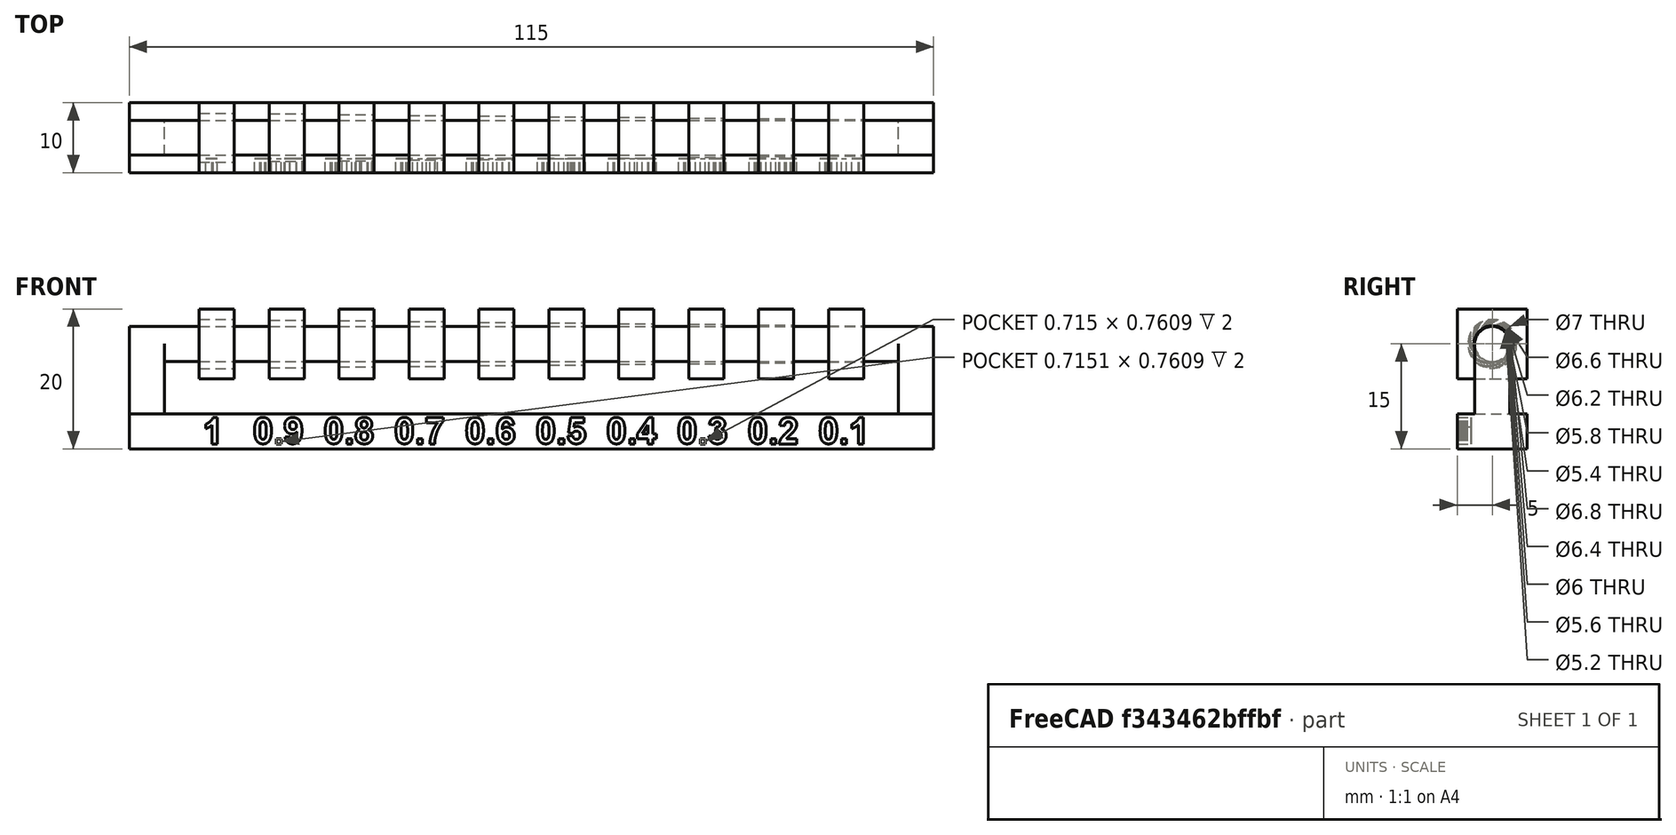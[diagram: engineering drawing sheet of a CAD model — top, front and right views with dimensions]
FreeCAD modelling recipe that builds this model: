
FCSTD DOCUMENT  (FreeCAD 0.18.3R)
Label: clearance
License: All rights reserved
LicenseURL: http://en.wikipedia.org/wiki/All_rights_reserved
objects: Part::Box×13, Part::Cylinder×11, Part::Cut×11, Part::MultiFuse×1, Part::Part2DObjectPython×1, Part::Extrusion×1
note: 38 computed .brp shape members not serialized (recipe doc carries the construction recipe); baked Part::Feature solids carry a one-line shape summary decoded from their .brp

FEATURE [Part::Box] Box  label="leg 0"
  AttacherType = Attacher::AttachEngine3D
  Height = 10
  Length = 5
  Width = 5
FEATURE [Part::Cylinder] Cylinder  label="axel"
  Angle = 360
  AttacherType = Attacher::AttachEngine3D
  Height = 115
  Placement = pos=(0,2.5,10) rot=(0,1,0;1.5708rad)
  Radius = 2.5
FEATURE [Part::Box] Box001  label="leg 1"
  AttacherType = Attacher::AttachEngine3D
  Height = 10
  Length = 5
  Placement = pos=(110,0,0) rot=(0,0,1;0rad)
  Width = 5
FEATURE [Part::Box] Box002  label="1 body"
  AttacherType = Attacher::AttachEngine3D
  Height = 10
  Length = 5
  Placement = pos=(10,-2.5,5) rot=(0,0,1;0rad)
  Width = 10
FEATURE [Part::Cylinder] Cylinder001  label="1 clearance"
  Angle = 360
  AttacherType = Attacher::AttachEngine3D
  Height = 115
  Placement = pos=(0,2.5,10) rot=(0,1,0;1.5708rad)
  Radius = 3.5
FEATURE [Part::Cut] Cut  label="1"
  Base = -> Box002
  Tool = -> Cylinder001
FEATURE [Part::Box] Box003  label="base"
  AttacherType = Attacher::AttachEngine3D
  Height = 5
  Length = 115
  Placement = pos=(0,-2.5,-5) rot=(0,0,1;0rad)
  Width = 10
FEATURE [Part::Box] Box004  label="0.8 body"
  AttacherType = Attacher::AttachEngine3D
  Height = 10
  Length = 5
  Placement = pos=(30,-2.5,5) rot=(0,0,1;0rad)
  Width = 10
FEATURE [Part::Cylinder] Cylinder002  label="0.8 clearance"
  Angle = 360
  AttacherType = Attacher::AttachEngine3D
  Height = 115
  Placement = pos=(0,2.5,10) rot=(0,1,0;1.5708rad)
  Radius = 3.3
FEATURE [Part::Cut] Cut001  label="0.8"
  Base = -> Box004
  Tool = -> Cylinder002
FEATURE [Part::Box] Box005  label="0.6 body"
  AttacherType = Attacher::AttachEngine3D
  Height = 10
  Length = 5
  Placement = pos=(50,-2.5,5) rot=(0,0,1;0rad)
  Width = 10
FEATURE [Part::Cylinder] Cylinder003  label="0.6 clearance"
  Angle = 360
  AttacherType = Attacher::AttachEngine3D
  Height = 115
  Placement = pos=(0,2.5,10) rot=(0,1,0;1.5708rad)
  Radius = 3.1
FEATURE [Part::Cut] Cut002  label="0.6"
  Base = -> Box005
  Tool = -> Cylinder003
FEATURE [Part::Cylinder] Cylinder004  label="0.4 clearance"
  Angle = 360
  AttacherType = Attacher::AttachEngine3D
  Height = 115
  Placement = pos=(0,2.5,10) rot=(0,1,0;1.5708rad)
  Radius = 2.9
FEATURE [Part::Box] Box006  label="0.4 body"
  AttacherType = Attacher::AttachEngine3D
  Height = 10
  Length = 5
  Placement = pos=(70,-2.5,5) rot=(0,0,1;0rad)
  Width = 10
FEATURE [Part::Cut] Cut003  label="0.4"
  Base = -> Box006
  Tool = -> Cylinder004
FEATURE [Part::Cylinder] Cylinder005  label="0.2 clearance"
  Angle = 360
  AttacherType = Attacher::AttachEngine3D
  Height = 115
  Placement = pos=(0,2.5,10) rot=(0,1,0;1.5708rad)
  Radius = 2.7
FEATURE [Part::Box] Box007  label="0.2 body"
  AttacherType = Attacher::AttachEngine3D
  Height = 10
  Length = 5
  Placement = pos=(90,-2.5,5) rot=(0,0,1;0rad)
  Width = 10
FEATURE [Part::Cut] Cut004  label="0.2"
  Base = -> Box007
  Tool = -> Cylinder005
FEATURE [Part::Cylinder] Cylinder006  label="0.9 clearance"
  Angle = 360
  AttacherType = Attacher::AttachEngine3D
  Height = 115
  Placement = pos=(0,2.5,10) rot=(0,1,0;1.5708rad)
  Radius = 3.4
FEATURE [Part::Box] Box008  label="0.9 body"
  AttacherType = Attacher::AttachEngine3D
  Height = 10
  Length = 5
  Placement = pos=(20,-2.5,5) rot=(0,0,1;0rad)
  Width = 10
FEATURE [Part::Cut] Cut006  label="0.9"
  Base = -> Box008
  Tool = -> Cylinder006
FEATURE [Part::Cylinder] Cylinder007  label="0.7 clearance"
  Angle = 360
  AttacherType = Attacher::AttachEngine3D
  Height = 115
  Placement = pos=(0,2.5,10) rot=(0,1,0;1.5708rad)
  Radius = 3.2
FEATURE [Part::Box] Box009  label="0.7 body"
  AttacherType = Attacher::AttachEngine3D
  Height = 10
  Length = 5
  Placement = pos=(40,-2.5,5) rot=(0,0,1;0rad)
  Width = 10
FEATURE [Part::Cut] Cut007  label="0.7"
  Base = -> Box009
  Tool = -> Cylinder007
FEATURE [Part::Cylinder] Cylinder008  label="0.5 clearance"
  Angle = 360
  AttacherType = Attacher::AttachEngine3D
  Height = 115
  Placement = pos=(0,2.5,10) rot=(0,1,0;1.5708rad)
  Radius = 3
FEATURE [Part::Box] Box010  label="0.5 body"
  AttacherType = Attacher::AttachEngine3D
  Height = 10
  Length = 5
  Placement = pos=(60,-2.5,5) rot=(0,0,1;0rad)
  Width = 10
FEATURE [Part::Cut] Cut008  label="0.5"
  Base = -> Box010
  Tool = -> Cylinder008
FEATURE [Part::Cylinder] Cylinder009  label="0.3 cearance"
  Angle = 360
  AttacherType = Attacher::AttachEngine3D
  Height = 115
  Placement = pos=(0,2.5,10) rot=(0,1,0;1.5708rad)
  Radius = 2.8
FEATURE [Part::Box] Box011  label="0.3 body"
  AttacherType = Attacher::AttachEngine3D
  Height = 10
  Length = 5
  Placement = pos=(80,-2.5,5) rot=(0,0,1;0rad)
  Width = 10
FEATURE [Part::Cut] Cut009  label="0.3"
  Base = -> Box011
  Tool = -> Cylinder009
FEATURE [Part::Cylinder] Cylinder010  label="0.1 clearance"
  Angle = 360
  AttacherType = Attacher::AttachEngine3D
  Height = 115
  Placement = pos=(0,2.5,10) rot=(0,1,0;1.5708rad)
  Radius = 2.6
FEATURE [Part::Box] Box012  label="0.1 body"
  AttacherType = Attacher::AttachEngine3D
  Height = 10
  Length = 5
  Placement = pos=(100,-2.5,5) rot=(0,0,1;0rad)
  Width = 10
FEATURE [Part::Cut] Cut010  label="0.1"
  Base = -> Box012
  Tool = -> Cylinder010
FEATURE [Part::MultiFuse] Fusion  label="clearances"
  Shapes = -> [Box,Cylinder,Box001,Cut,Box003,Cut001,Cut002,Cut003,Cut004,Cut006,Cut007,Cut008,Cut009,Cut010]
FEATURE [Part::Part2DObjectPython] ShapeString  # Draft 2D object (typed FeaturePython)
  FontFile = <userpath>/git/aws2/bin/fonts/Arial Bold.ttf
  Placement = pos=(10.5,-2.5,-4.3) rot=(1,0,0;1.5708rad)
  Size = 4
  String = 1   0.9  0.8  0.7  0.6  0.5  0.4  0.3  0.2  0.1
  Support = -> [Fusion]
  Tracking = 0
FEATURE [Part::Extrusion] Extrude
  Base = -> ShapeString
  Dir = (0,-1,2e-16)
  DirMode = 2
  FaceMakerClass = Part::FaceMakerBullseye
  LengthFwd = -2
  LengthRev = 0
  Solid = false
  Symmetric = false
FEATURE [Part::Cut] Cut005  label="labeled"
  Base = -> Fusion
  Tool = -> Extrude
